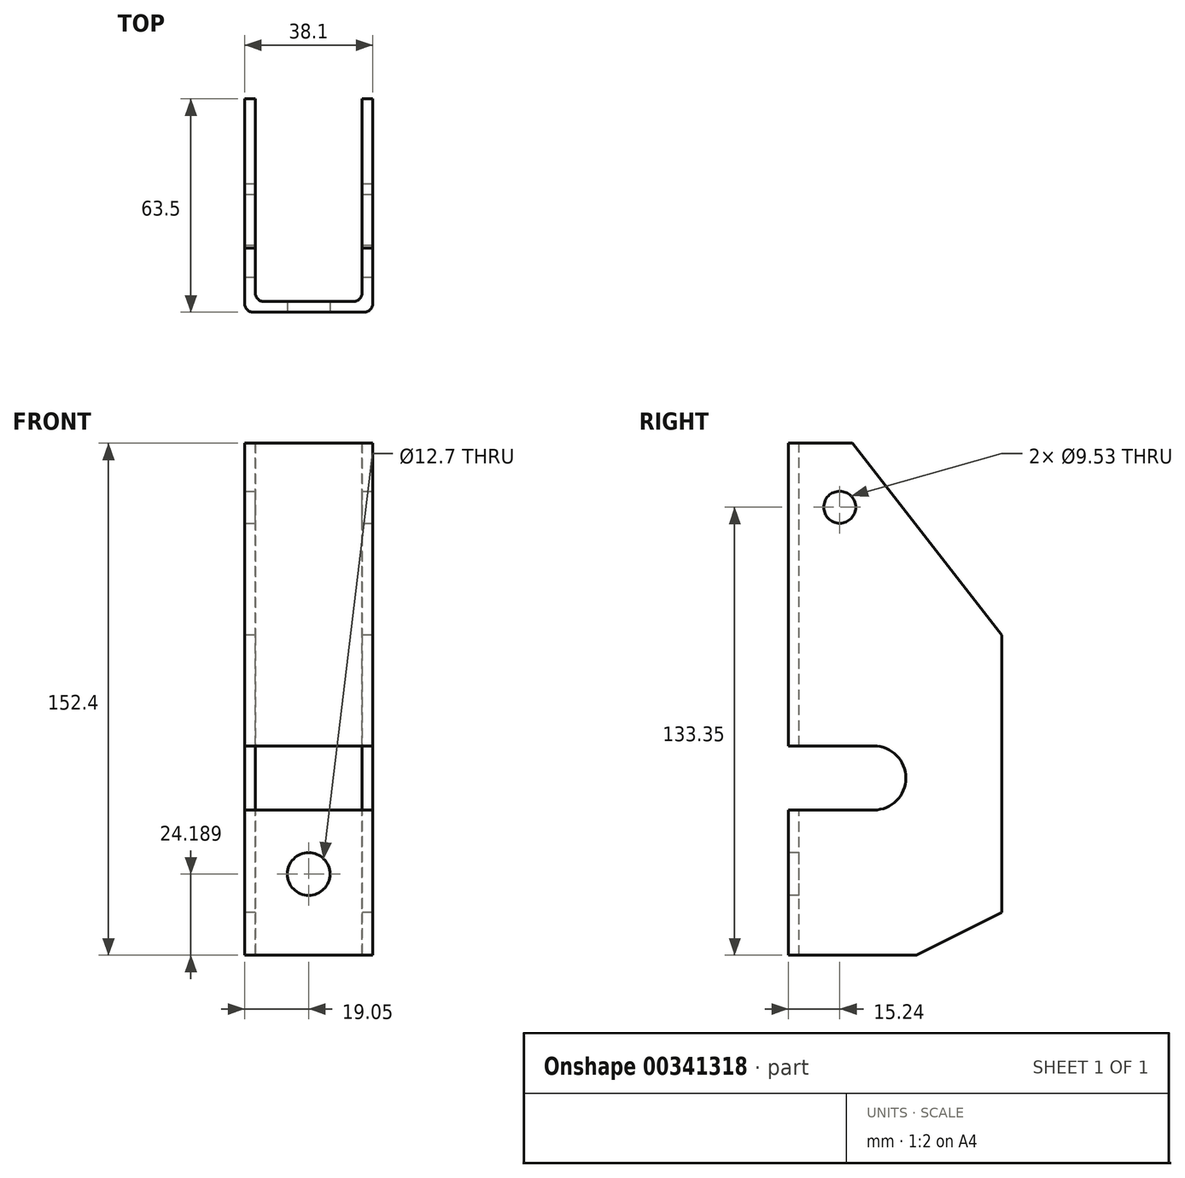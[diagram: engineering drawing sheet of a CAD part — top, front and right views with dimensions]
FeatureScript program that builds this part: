
annotation { "Feature Type Name" : "Feature", "Feature Type Description" : "" }
export const myFeature = defineFeature(function(context is Context, id is Id, definition is map)
    precondition{}
    {
        {
            var Q0;
            Q0=qCreatedBy(makeId("Right.planeOp"),FACE);
            var sketch = newSketch(context, id + "F0", { "sketchPlane" : qUnion([Q0])});
            skLineSegment(sketch, "E0.bottom", {"start": v(-76.2, 76.2) * mm, "end": v(-57.15, 76.2) * mm});
            skLineSegment(sketch, "E0.top", {"start": v(-76.2, -76.2) * mm, "end": v(-38.1, -76.2) * mm});
            skPoint(sketch, "E0.middle", {"position": v(0, 0) * mm});
            skLineSegment(sketch, "E1", {"start": v(-57.15, 76.2) * mm, "end": v(-12.7, 19.05) * mm});
            skLineSegment(sketch, "E2", {"start": v(-12.7, 19.05) * mm, "end": v(-12.7, -63.5) * mm});
            skLineSegment(sketch, "E3", {"start": v(-12.7, -63.5) * mm, "end": v(-38.1, -76.2) * mm});
            skPoint(sketch, "E0.right.end.orphan", {"position": v(76.2, -76.2) * mm});
            skPoint(sketch, "E0.right.start.orphan", {"position": v(76.2, 76.2) * mm});
            skArc(sketch, "E4", {"start": v(-50.8, -32.96) * mm, "mid": v(-41.28, -23.44) * mm, "end": v(-50.8, -13.91) * mm});
            skLineSegment(sketch, "E5", {"start": v(-50.8, -13.91) * mm, "end": v(-76.2, -13.91) * mm});
            skLineSegment(sketch, "E6", {"start": v(-50.8, -32.96) * mm, "end": v(-76.2, -32.96) * mm});
            skLineSegment(sketch, "E7.trimOffspring", {"start": v(-76.2, -32.96) * mm, "end": v(-76.2, -76.2) * mm});
            skLineSegment(sketch, "E8", {"start": v(-76.2, 76.2) * mm, "end": v(-76.2, -13.91) * mm});
            skSolve(sketch);
        }
        {
            var Q0;
            Q0 = qSketchRegion(id + "F0", true);
            extrude(context, id + "F1", {"entities" : qUnion([Q0]), "depth" : 38.1 * mm});
        }
        {
            var Q0;
            Q0=makeQuery(id+"F1.opExtrude","SWEPT_FACE",FACE,{"disambiguationData":[OSD([sQuery(id+"F0.wireOp",EDGE,"E0.bottom")])]});
            var sketch = newSketch(context, id + "F2", { "sketchPlane" : qUnion([Q0])});
            skLineSegment(sketch, "E9.bottom", {"start": v(3.18, -73.02) * mm, "end": v(34.93, -73.02) * mm});
            skLineSegment(sketch, "E9.top", {"start": v(3.18, 0) * mm, "end": v(34.93, 0) * mm});
            skLineSegment(sketch, "E9.left", {"start": v(3.18, -73.02) * mm, "end": v(3.18, 0) * mm});
            skLineSegment(sketch, "E9.right", {"start": v(34.93, -73.02) * mm, "end": v(34.93, 0) * mm});
            skSolve(sketch);
        }
        {
            var Q0;
            Q0 = qSketchRegion(id + "F2", true);
            extrude(context, id + "F3", {"entities" : qUnion([Q0]), "operationType" : NewBodyOperationType.REMOVE, "endBound" : BoundingType.THROUGH_ALL, "oppositeDirection" : true, "depth" : 25.4 * mm});
        }
        {
            var Q0;
            {var subQ0=sQuery(id+"F2.wireOp",EDGE,"E9.bottom");var subQ1=sQuery(id+"F2.wireOp",EDGE,"E9.left");Q0=makeQuery(id+"F3.boolean.opBoolean","COPY",EDGE,{"disambiguationData":[TD([makeQuery(id+"F1.opExtrude","SWEPT_FACE",FACE,{"disambiguationData":[OSD([sQuery(id+"F0.wireOp",EDGE,"E0.bottom")])]})])],"derivedFrom":makeQuery(id+"F3.opExtrude","SWEPT_EDGE",EDGE,{"disambiguationData":[OSD([subQ0,subQ1])]})});}
            var Q1;
            {var subQ0=sQuery(id+"F2.wireOp",EDGE,"E9.bottom");var subQ1=sQuery(id+"F2.wireOp",EDGE,"E9.right");Q1=makeQuery(id+"F3.boolean.opBoolean","COPY",EDGE,{"disambiguationData":[TD([makeQuery(id+"F1.opExtrude","SWEPT_FACE",FACE,{"disambiguationData":[OSD([sQuery(id+"F0.wireOp",EDGE,"E0.bottom")])]})])],"derivedFrom":makeQuery(id+"F3.opExtrude","SWEPT_EDGE",EDGE,{"disambiguationData":[OSD([subQ0,subQ1])]})});}
            var Q2;
            {var subQ0=sQuery(id+"F2.wireOp",EDGE,"E9.bottom");var subQ1=sQuery(id+"F2.wireOp",EDGE,"E9.right");Q2=makeQuery(id+"F3.boolean.opBoolean","COPY",EDGE,{"disambiguationData":[TD([makeQuery(id+"F1.opExtrude","SWEPT_FACE",FACE,{"disambiguationData":[OSD([sQuery(id+"F0.wireOp",EDGE,"E0.top")])]})])],"derivedFrom":makeQuery(id+"F3.opExtrude","SWEPT_EDGE",EDGE,{"disambiguationData":[OSD([subQ0,subQ1])]})});}
            var Q3;
            {var subQ0=sQuery(id+"F2.wireOp",EDGE,"E9.bottom");var subQ1=sQuery(id+"F2.wireOp",EDGE,"E9.left");Q3=makeQuery(id+"F3.boolean.opBoolean","COPY",EDGE,{"disambiguationData":[TD([makeQuery(id+"F1.opExtrude","SWEPT_FACE",FACE,{"disambiguationData":[OSD([sQuery(id+"F0.wireOp",EDGE,"E0.top")])]})])],"derivedFrom":makeQuery(id+"F3.opExtrude","SWEPT_EDGE",EDGE,{"disambiguationData":[OSD([subQ0,subQ1])]})});}
            fillet(context, id + "F4", {"entities" : qUnion([Q0, Q1, Q2, Q3]), "radius" : 2.54 * mm, "tangentPropagation" : true, "allowEdgeOverflow" : false});
        }
        {
            var Q0;
            Q0=makeQuery(id+"F1.opExtrude","CAP_EDGE",EDGE,{"disambiguationData":[OSD([sQuery(id+"F0.wireOp",EDGE,"E7.trimOffspring")])],"isStart":false});
            var Q1;
            Q1=makeQuery(id+"F1.opExtrude","CAP_EDGE",EDGE,{"disambiguationData":[OSD([sQuery(id+"F0.wireOp",EDGE,"E7.trimOffspring")])],"isStart":true});
            var Q2;
            Q2=makeQuery(id+"F1.opExtrude","CAP_EDGE",EDGE,{"disambiguationData":[OSD([sQuery(id+"F0.wireOp",EDGE,"E8")])],"isStart":true});
            var Q3;
            Q3=makeQuery(id+"F1.opExtrude","CAP_EDGE",EDGE,{"disambiguationData":[OSD([sQuery(id+"F0.wireOp",EDGE,"E8")])],"isStart":false});
            fillet(context, id + "F5", {"entities" : qUnion([Q0, Q1, Q2, Q3]), "radius" : 2.54 * mm, "tangentPropagation" : true, "allowEdgeOverflow" : false});
        }
        {
            var Q0;
            Q0=makeQuery(id+"F1.opExtrude","SWEPT_FACE",FACE,{"disambiguationData":[OSD([sQuery(id+"F0.wireOp",EDGE,"E7.trimOffspring")])]});
            var sketch = newSketch(context, id + "F6", { "sketchPlane" : qUnion([Q0])});
            skCircle(sketch, "E10", {"center": v(19.05, -52.01) * mm, "radius": 6.35 * mm});
            skPoint(sketch, "E10.centerSnap0", {"position": v(19.05, -32.96) * mm});
            skSolve(sketch);
        }
        {
            var Q0;
            Q0 = qSketchRegion(id + "F6", true);
            extrude(context, id + "F7", {"entities" : qUnion([Q0]), "operationType" : NewBodyOperationType.REMOVE, "oppositeDirection" : true, "depth" : 25.4 * mm});
        }
        {
            var Q0;
            Q0=makeQuery(id+"F1.opExtrude","CAP_FACE",FACE,{"disambiguationData":[OSD([sQuery(id+"F0.wireOp",EDGE,"E0.bottom"),sQuery(id+"F0.wireOp",EDGE,"E0.top"),sQuery(id+"F0.wireOp",EDGE,"E1"),sQuery(id+"F0.wireOp",EDGE,"E2"),sQuery(id+"F0.wireOp",EDGE,"E3"),sQuery(id+"F0.wireOp",EDGE,"E4"),sQuery(id+"F0.wireOp",EDGE,"E5"),sQuery(id+"F0.wireOp",EDGE,"E6"),sQuery(id+"F0.wireOp",EDGE,"E7.trimOffspring"),sQuery(id+"F0.wireOp",EDGE,"E8")])],"isStart":false});
            var sketch = newSketch(context, id + "F8", { "sketchPlane" : qUnion([Q0])});
            skCircle(sketch, "E11", {"center": v(-60.96, 57.15) * mm, "radius": 4.76 * mm});
            skSolve(sketch);
        }
        {
            var Q0;
            Q0 = qSketchRegion(id + "F8", true);
            extrude(context, id + "F9", {"entities" : qUnion([Q0]), "operationType" : NewBodyOperationType.REMOVE, "endBound" : BoundingType.THROUGH_ALL, "oppositeDirection" : true, "depth" : 19.05 * mm});
        }
    });
